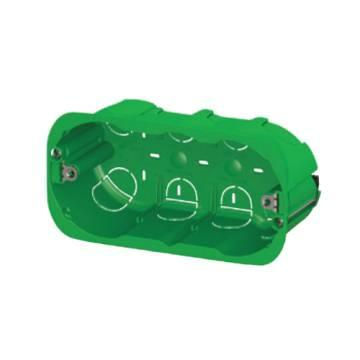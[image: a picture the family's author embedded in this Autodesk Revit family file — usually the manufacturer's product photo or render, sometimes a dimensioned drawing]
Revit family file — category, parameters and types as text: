
# Revit family: Building-FlushMountingEnclosures-GEWISS-24SC-GREENWALL-BOXES_4P
name_source: partatom
category: Apparecchi elettrici
revit_build: Autodesk Revit 2016 (Build: 20161004_0715(x64)
units: mm (PartAtom-declared; Revit-internal decimal feet)

## family parameters
Condiviso = Sì
Host = Superficie
Mantenere orientamento annotazione = Sì
Numero OmniClass = 23.80.30.14.24
Punto di calcolo locali = Sì
Quota connettore circolare = Usa diametro
Taglio con vuoti quando caricato = Sì
Tipo di parte = Normale
Titolo OmniClass = Junction Boxes

## types (1)
- GW24404PM - Halogen free - 4P
    Catalogue = BUILDING
    Catalogue Range = 24SC
    Characteristics = Halogen free
    Compartment pre-arrangement = 2
    Description: = 4 gang
    Descrizione = PLASTERBOARD W. 4 GANG F.M.BOX - GW
    EAN code = 8011564801929
    Electrocod = 0210
    Elementi acciaio = GEWISS - Elementi acciaio
    Fixing supports axles distance = 108,5MM
    For walls = Plasterboard
    Glow Wire Test = 850°C
    IDF = cd257564-4306-4429-a883-b7388f9310d0
    IDT = ced4c316-61fc-4ec6-8ed7-dfe497302916
    IP degree = IP40
    Immagine tipo = GW24404PM.jpg
    Installation = Flush mounting enclosures
    Modello = GW24404PM
    No. SYSTEM modules = 4 gang
    Operating temperature = -15 ÷ +60°C
    Outer dim. LxHxD (mm) = 133x73x50
    Produttore = GEWISS S.p.A.
    Prospetto di default = 1219.2 mm  [stored 4 ft]
    SEO = Box
    Scatola = GEWISS - scatola a incasso
    Shock resistance = IK07
    Technical sheet = https://www.gewiss.com
    Thermo-pressure with ball = 70
    Type of material = Halogen free with Standard EN 50267-2-2
    Type: = High capacity
    URL = https://www.gewiss.com
    Version file RFA = 19.0

note: source unit labels omitted for Thermo-pressure with ball — the stored unit's dimension contradicts the parameter name (converter mislabeling)

note: [stored X ft] marks values corroborated as IEEE doubles in the binary element streams (Revit-internal decimal feet)

## geometry (parser evidence)
native form markers: Blend x2, Sweep x3
no freeform markers — native parametric forms only
